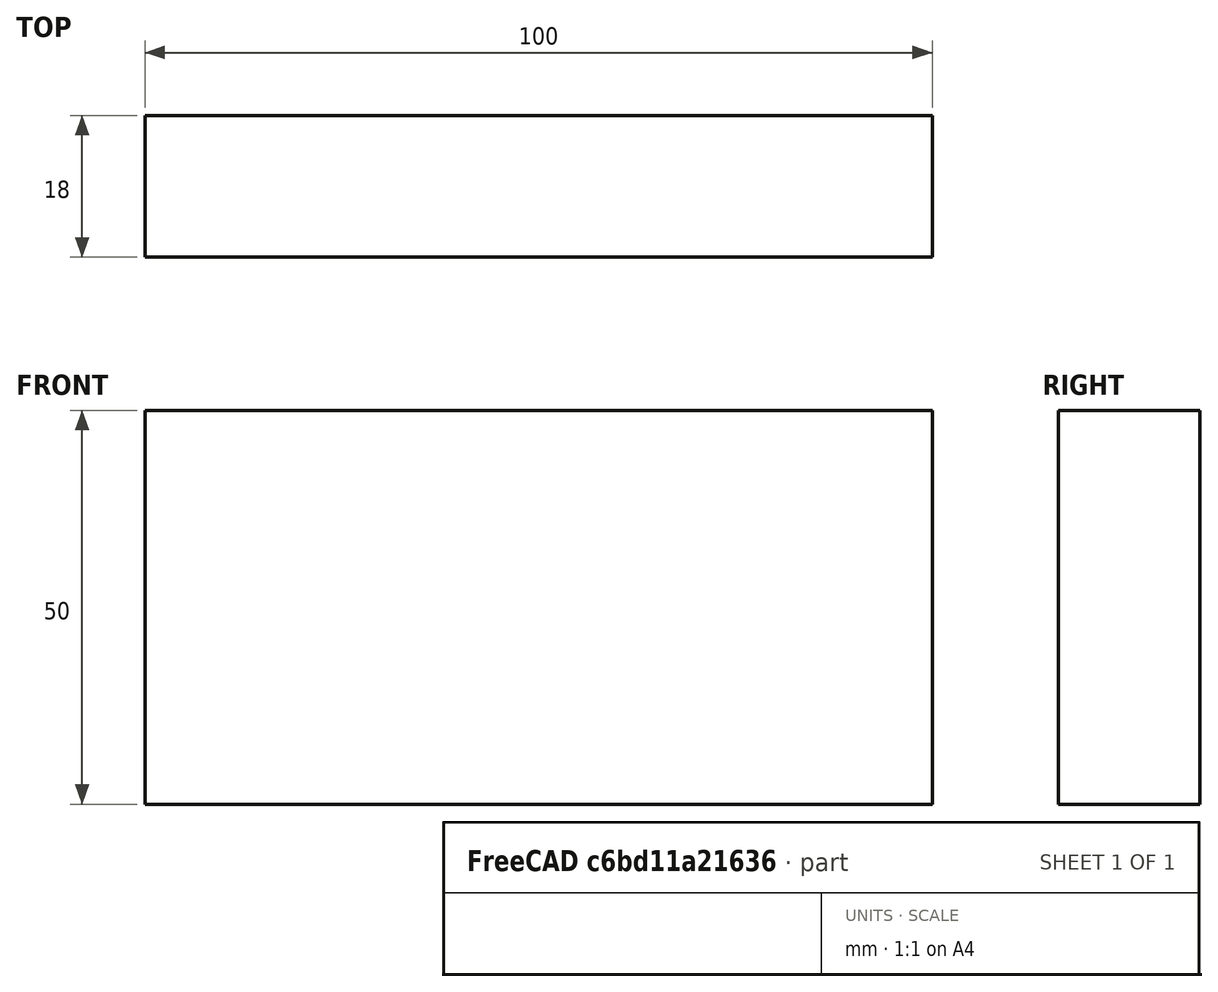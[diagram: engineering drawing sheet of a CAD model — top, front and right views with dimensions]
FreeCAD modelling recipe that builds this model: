
FCSTD DOCUMENT  (FreeCAD 0.15R4671 (Git))
Label: Flat Bar 100x18 EN10058 S235JR
License: All rights reserved
LicenseURL: http://en.wikipedia.org/wiki/All_rights_reserved
objects: Sketcher::SketchObject×1, Part::Extrusion×1
note: 2 computed .brp shape members not serialized (recipe doc carries the construction recipe); baked Part::Feature solids carry a one-line shape summary decoded from their .brp

FEATURE [Sketcher::SketchObject] Sketch
  sketch-geometry (4):
    g0: LineSegment StartX=-50 StartY=-9 StartZ=0 EndX=50 EndY=-9 EndZ=0
    g1: LineSegment StartX=50 StartY=-9 StartZ=0 EndX=50 EndY=9 EndZ=0
    g2: LineSegment StartX=50 StartY=9 StartZ=0 EndX=-50 EndY=9 EndZ=0
    g3: LineSegment StartX=-50 StartY=9 StartZ=0 EndX=-50 EndY=-9 EndZ=0
  constraints (12):
    c: Coincident(g0,g1)
    c: Coincident(g1,g2)
    c: Coincident(g2,g3)
    c: Coincident(g3,g0)
    c: Horizontal(g0)
    c: Horizontal(g2)
    c: Vertical(g1)
    c: Vertical(g3)
    c: Symmetric(g1,g2,g-2)
    c: Symmetric(g0,g1,g-1)
    c: DistanceY(g1) = 18
    c: DistanceX(g0) = 100
FEATURE [Part::Extrusion] Extrude  label="Flat Bar 100x18 EN10058 S235JR"
  Base = -> Sketch
  Dir = (0,0,50)
  Solid = true
